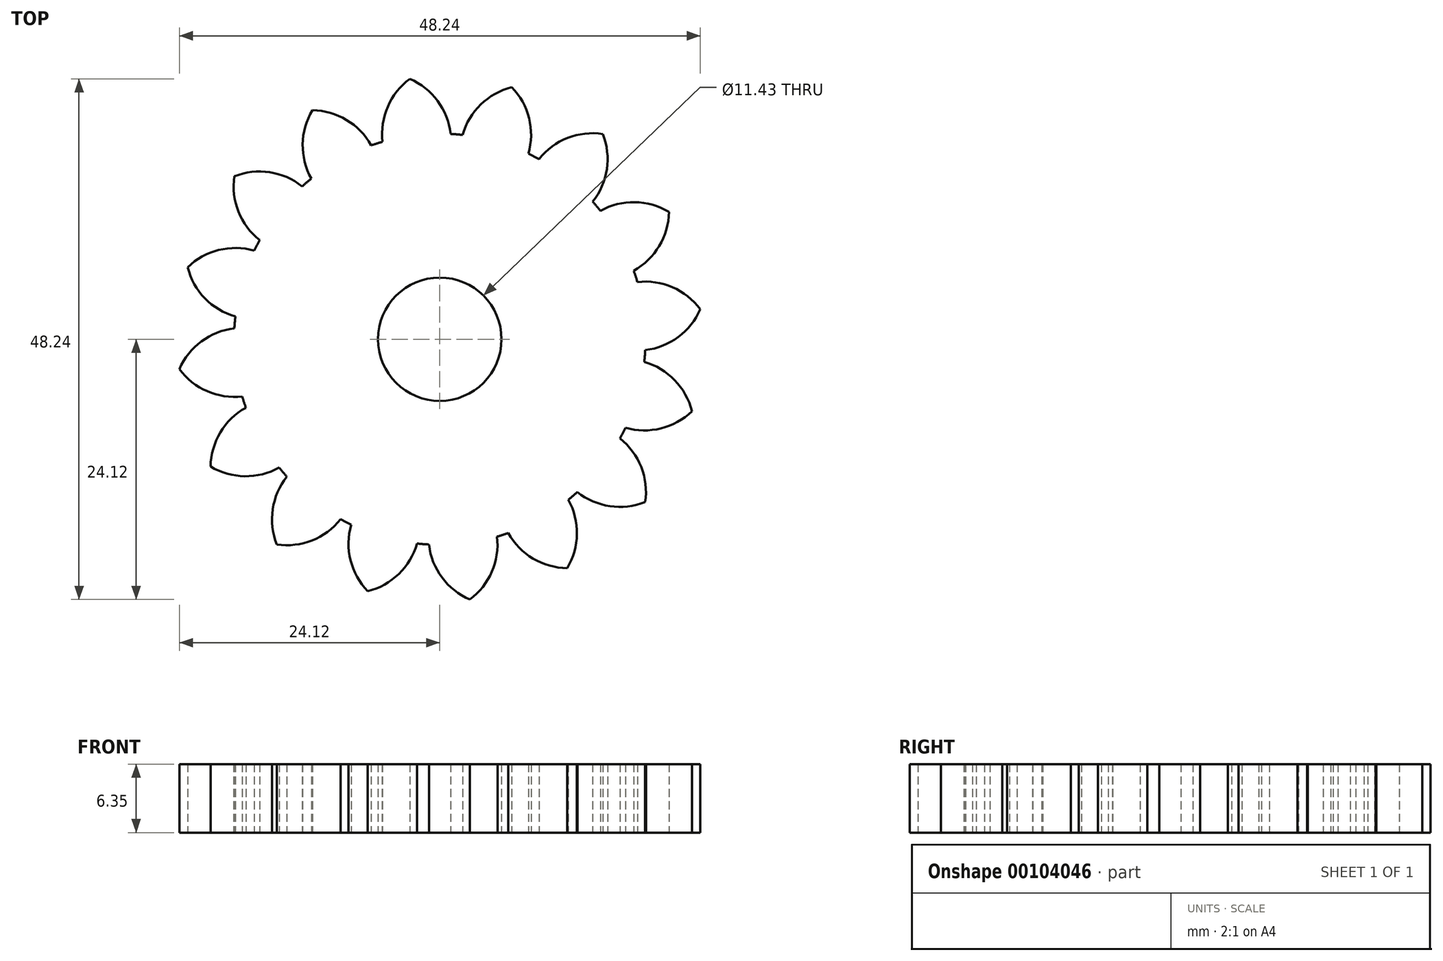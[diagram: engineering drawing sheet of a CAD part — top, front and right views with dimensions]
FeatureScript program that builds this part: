
annotation { "Feature Type Name" : "Feature", "Feature Type Description" : "" }
export const myFeature = defineFeature(function(context is Context, id is Id, definition is map)
    precondition{}
    {
        {
            var Q0;
            Q0=qCreatedBy(makeId("Top.planeOp"),FACE);
            var sketch = newSketch(context, id + "F0", { "sketchPlane" : qUnion([Q0])});
            skCircle(sketch, "E0", {"center": v(0, 0) * mm, "radius": 19.05 * mm});
            skArc(sketch, "E1", {"start": v(-6.35, 17.96) * mm, "mid": v(-8.64, 20.32) * mm, "end": v(-11.8, 21.22) * mm});
            skArc(sketch, "E2", {"start": v(-11.8, 21.22) * mm, "mid": v(-12.7, 18.06) * mm, "end": v(-11.9, 14.88) * mm});
            skCircle(sketch, "E3", {"center": v(0, 0) * mm, "radius": 5.72 * mm});
            skSolve(sketch);
        }
        {
            var Q0;
            Q0 = qSketchRegion(id + "F0", true);
            extrude(context, id + "F1", {"entities" : qUnion([Q0]), "depth" : 6.35 * mm});
        }
        {
            var Q0;
            Q0=makeQuery(id+"F1.opExtrude","SWEPT_BODY",BODY,{"disambiguationData":[OSD([sQuery(id+"F0.wireOp",EDGE,"E0"),sQuery(id+"F0.wireOp",EDGE,"E1"),sQuery(id+"F0.wireOp",EDGE,"E2"),sQuery(id+"F0.wireOp",EDGE,"E3")])]});
            var Q1;
            Q1=makeQuery(id+"F1.opExtrude","SWEPT_FACE",FACE,{"disambiguationData":[OSD([sQuery(id+"F0.wireOp",EDGE,"E0")])]});
            circularPattern(context, id + "F2", {"operationType" : NewBodyOperationType.ADD, "entities" : qUnion([Q0]), "axis" : qUnion([Q1]), "angle" : 360 * degree, "instanceCount" : 16, "equalSpace" : true});
        }
    });
